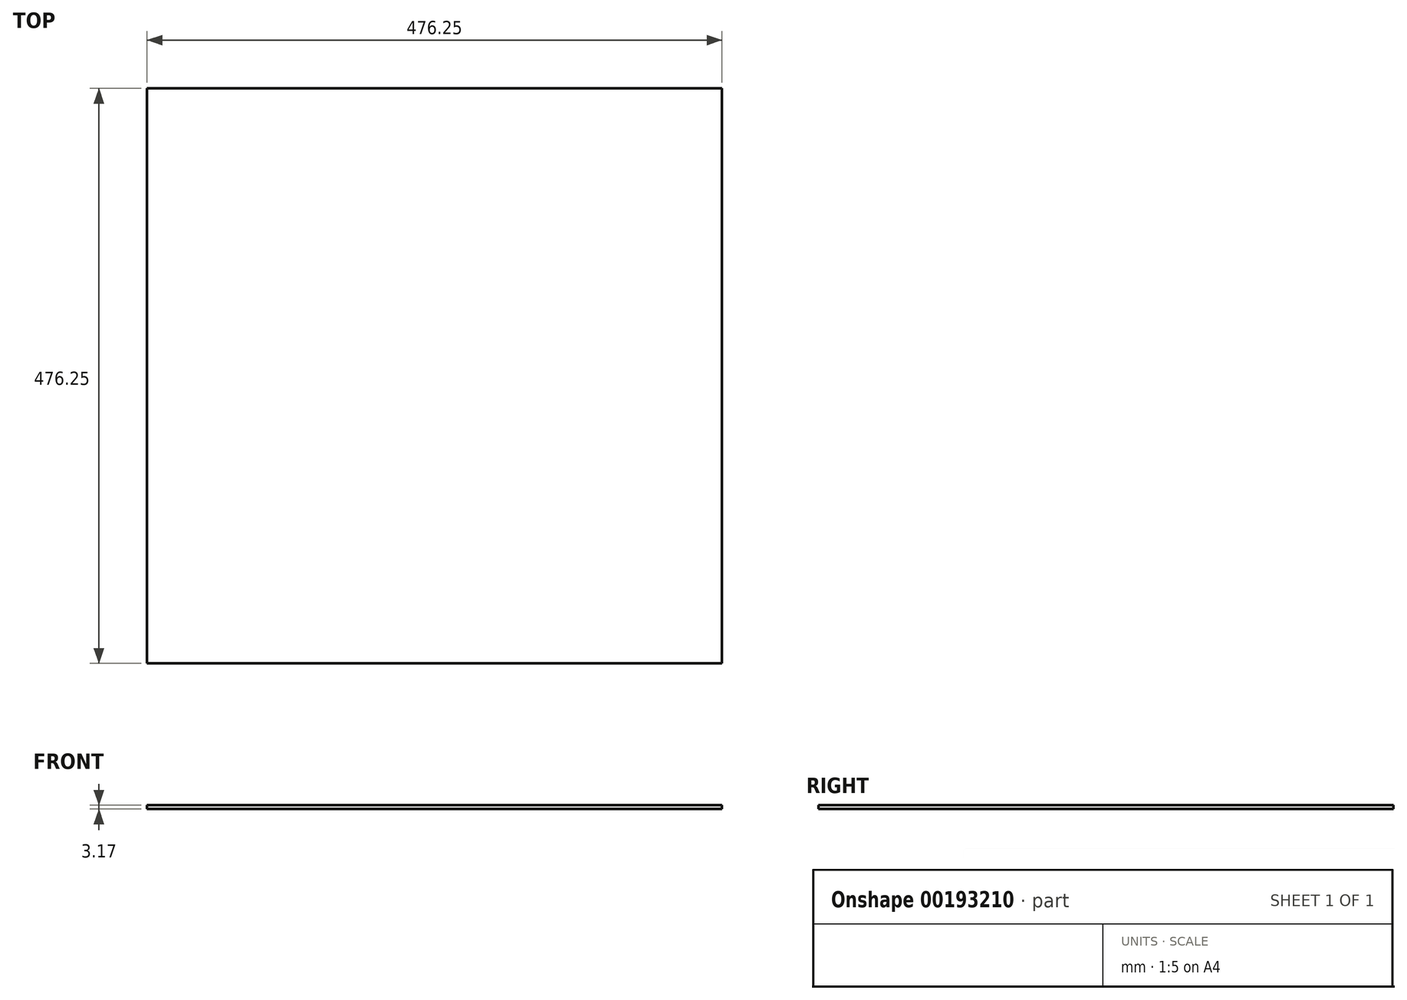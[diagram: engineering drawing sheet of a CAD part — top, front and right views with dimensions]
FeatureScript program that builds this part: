
annotation { "Feature Type Name" : "Feature", "Feature Type Description" : "" }
export const myFeature = defineFeature(function(context is Context, id is Id, definition is map)
    precondition{}
    {
        {
            var Q0;
            Q0=qCreatedBy(makeId("Top.planeOp"),FACE);
            var sketch = newSketch(context, id + "F0", { "sketchPlane" : qUnion([Q0])});
            skLineSegment(sketch, "E0.bottom", {"start": v(0, 0) * mm, "end": v(476.25, 0) * mm});
            skLineSegment(sketch, "E0.top", {"start": v(0, -476.25) * mm, "end": v(476.25, -476.25) * mm});
            skLineSegment(sketch, "E0.left", {"start": v(0, 0) * mm, "end": v(0, -476.25) * mm});
            skLineSegment(sketch, "E0.right", {"start": v(476.25, 0) * mm, "end": v(476.25, -476.25) * mm});
            skSolve(sketch);
        }
        {
            var Q0;
            Q0 = qSketchRegion(id + "F0", true);
            extrude(context, id + "F1", {"entities" : qUnion([Q0]), "depth" : 3.17 * mm});
        }
    });
